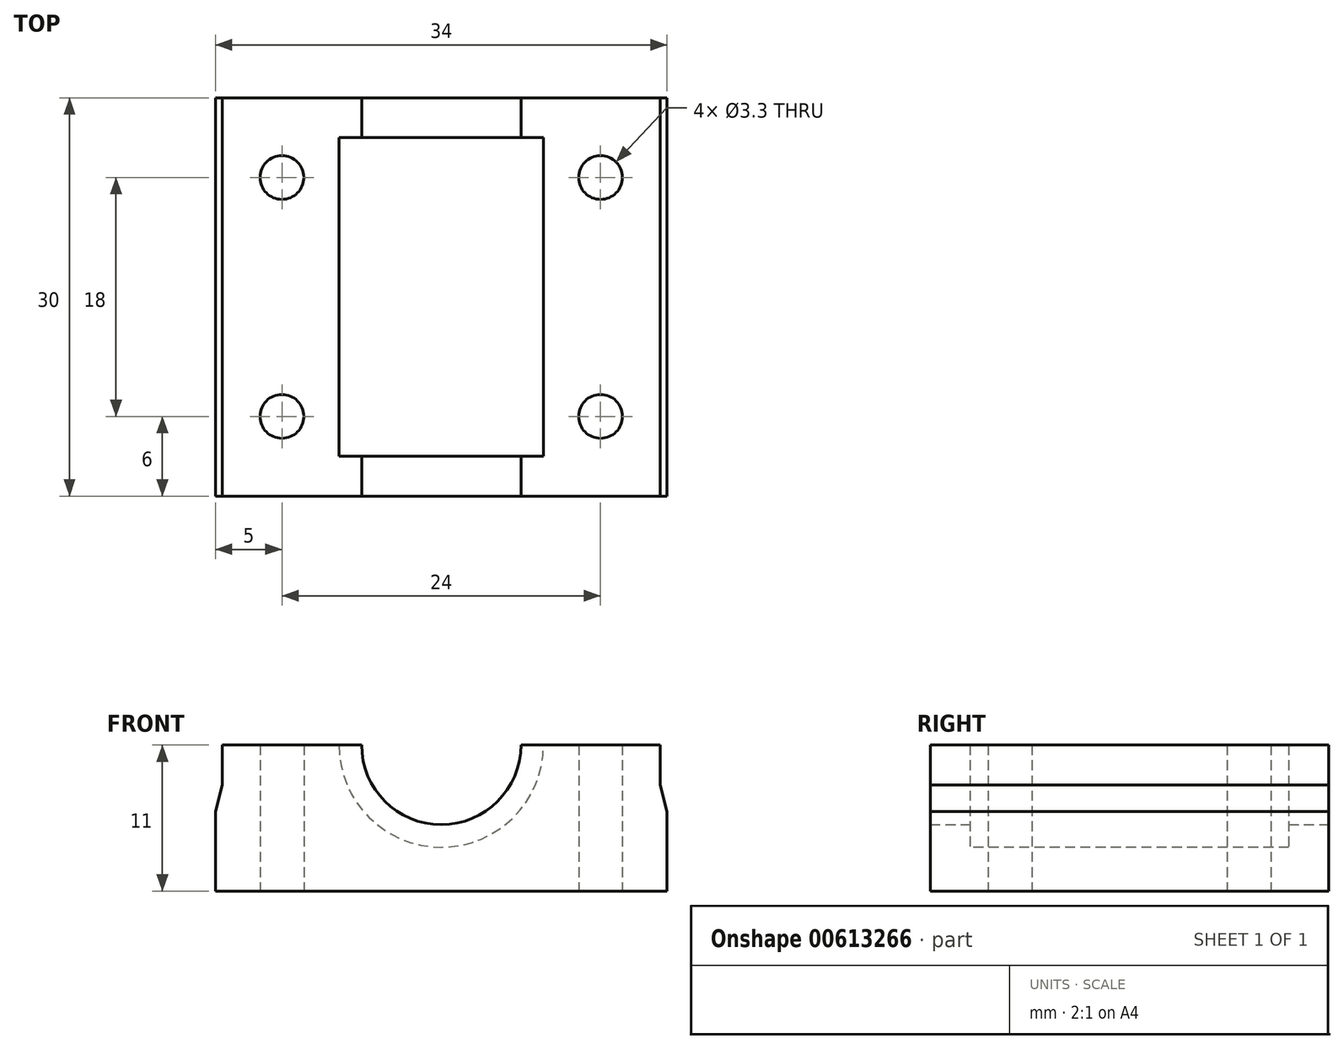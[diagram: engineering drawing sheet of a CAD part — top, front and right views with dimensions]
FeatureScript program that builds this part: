
annotation { "Feature Type Name" : "Feature", "Feature Type Description" : "" }
export const myFeature = defineFeature(function(context is Context, id is Id, definition is map)
    precondition{}
    {
        {
            var Q0;
            Q0=qCreatedBy(makeId("Front.planeOp"),FACE);
            var sketch = newSketch(context, id + "F0", { "sketchPlane" : qUnion([Q0])});
            skLineSegment(sketch, "E0", {"start": v(0, 0) * mm, "end": v(-5.45, 0) * mm});
            skLineSegment(sketch, "E1", {"start": v(-5.45, 0) * mm, "end": v(-9.5, 0) * mm});
            skLineSegment(sketch, "E2", {"start": v(-9.5, 0) * mm, "end": v(-17, 0) * mm});
            skLineSegment(sketch, "E3", {"start": v(-17, 0) * mm, "end": v(-17, 6) * mm});
            skLineSegment(sketch, "E4", {"start": v(-17, 6) * mm, "end": v(-16.5, 8) * mm});
            skLineSegment(sketch, "E5", {"start": v(-16.5, 8) * mm, "end": v(-16.5, 18) * mm});
            skLineSegment(sketch, "E6", {"start": v(-16.5, 18) * mm, "end": v(-9.5, 18) * mm});
            skLineSegment(sketch, "E7", {"start": v(-9.5, 18) * mm, "end": v(-3.5, 22) * mm});
            skLineSegment(sketch, "E8", {"start": v(-3.5, 22) * mm, "end": v(0, 22) * mm});
            skLineSegment(sketch, "E9", {"start": v(0, 22) * mm, "end": v(0, 0) * mm});
            skArc(sketch, "E10", {"start": v(0, 17) * mm, "mid": v(-6, 11) * mm, "end": v(0, 5) * mm});
            skLineSegment(sketch, "E11", {"start": v(-9.5, 29.22) * mm, "end": v(-9.5, -8.86) * mm, "construction": true});
            skLineSegment(sketch, "E12.MirrorCS", {"start": v(17, 6) * mm, "end": v(16.5, 8) * mm});
            skLineSegment(sketch, "E13.MirrorCS", {"start": v(0, 0) * mm, "end": v(5.45, 0) * mm});
            skLineSegment(sketch, "E14.MirrorCS", {"start": v(5.45, 0) * mm, "end": v(9.5, 0) * mm});
            skLineSegment(sketch, "E15.MirrorCS", {"start": v(9.5, 0) * mm, "end": v(17, 0) * mm});
            skLineSegment(sketch, "E16.MirrorCS", {"start": v(17, 0) * mm, "end": v(17, 6) * mm});
            skLineSegment(sketch, "E17.MirrorCS", {"start": v(16.5, 8) * mm, "end": v(16.5, 18) * mm});
            skLineSegment(sketch, "E18.MirrorCS", {"start": v(16.5, 18) * mm, "end": v(9.5, 18) * mm});
            skLineSegment(sketch, "E19.MirrorCS", {"start": v(9.5, 18) * mm, "end": v(3.5, 22) * mm});
            skLineSegment(sketch, "E20.MirrorCS", {"start": v(3.5, 22) * mm, "end": v(0, 22) * mm});
            skArc(sketch, "E21.MirrorCS", {"start": v(0, 17) * mm, "mid": v(6, 11) * mm, "end": v(0, 5) * mm});
            skCircle(sketch, "E22", {"center": v(0, 11) * mm, "radius": 7.5 * mm, "construction": true});
            skLineSegment(sketch, "E23", {"start": v(-16.5, 11) * mm, "end": v(16.5, 11) * mm});
            skLineSegment(sketch, "E24", {"start": v(-21.67, 8) * mm, "end": v(23.4, 8) * mm, "construction": true});
            skSolve(sketch);
        }
        {
            var Q0;
            {var subQ2=sQuery(id+"F0.wireOp",EDGE,"E0");Q0=makeQuery(id+"F0.imprint","IMPRINT",FACE,{"disambiguationData":[TD([[makeQuery(id+"F0.imprint","IMPRINT",EDGE,{"derivedFrom":subQ2}),-1.0]])]});}
            var Q1;
            Q1=makeQuery(id+"F0.imprint","IMPRINT",FACE,{"disambiguationData":[TD([[makeQuery(id+"F0.imprint","IMPRINT",EDGE,{"derivedFrom":sQuery(id+"F0.wireOp",EDGE,"E12.MirrorCS")}),1.0]])]});
            extrude(context, id + "F1", {"entities" : qUnion([Q0, Q1]), "endBound" : BoundingType.SYMMETRIC, "depth" : 30 * mm, "offsetDistance" : 25 * mm});
        }
        {
            var Q0;
            Q0=makeQuery(id+"F1.opExtrude","SWEPT_FACE",FACE,{"disambiguationData":[OSD([sQuery(id+"F0.wireOp",EDGE,"E2")])]});
            var sketch = newSketch(context, id + "F2", { "sketchPlane" : qUnion([Q0])});
            skPoint(sketch, "E25", {"position": v(-12, 9) * mm});
            skPoint(sketch, "E26", {"position": v(-12, -9) * mm});
            skPoint(sketch, "E27.MirrorP", {"position": v(12, 9) * mm});
            skPoint(sketch, "E28.MirrorP", {"position": v(12, -9) * mm});
            skLineSegment(sketch, "E29", {"start": v(-12, -30.48) * mm, "end": v(-12, 39.38) * mm, "construction": true});
            skSolve(sketch);
        }
        {
            var Q0;
            Q0=sQuery(id+"F2.wireOp",VERTEX,"E25");
            var Q1;
            Q1=sQuery(id+"F2.wireOp",VERTEX,"E26");
            var Q2;
            Q2=sQuery(id+"F2.wireOp",VERTEX,"E28.MirrorP");
            var Q3;
            Q3=sQuery(id+"F2.wireOp",VERTEX,"E27.MirrorP");
            var Q4;
            Q4=makeQuery(id+"F1.opExtrude","SWEPT_BODY",BODY,{"disambiguationData":[OSD([sQuery(id+"F0.wireOp",EDGE,"E0"),sQuery(id+"F0.wireOp",EDGE,"E1"),sQuery(id+"F0.wireOp",EDGE,"E2"),sQuery(id+"F0.wireOp",EDGE,"E3"),sQuery(id+"F0.wireOp",EDGE,"E4"),sQuery(id+"F0.wireOp",EDGE,"E5"),sQuery(id+"F0.wireOp",EDGE,"E6"),sQuery(id+"F0.wireOp",EDGE,"E7"),sQuery(id+"F0.wireOp",EDGE,"E8"),sQuery(id+"F0.wireOp",EDGE,"E10"),sQuery(id+"F0.wireOp",EDGE,"E12.MirrorCS"),sQuery(id+"F0.wireOp",EDGE,"E13.MirrorCS"),sQuery(id+"F0.wireOp",EDGE,"E14.MirrorCS"),sQuery(id+"F0.wireOp",EDGE,"E15.MirrorCS"),sQuery(id+"F0.wireOp",EDGE,"E16.MirrorCS"),sQuery(id+"F0.wireOp",EDGE,"E17.MirrorCS"),sQuery(id+"F0.wireOp",EDGE,"E18.MirrorCS"),sQuery(id+"F0.wireOp",EDGE,"E19.MirrorCS"),sQuery(id+"F0.wireOp",EDGE,"E20.MirrorCS"),sQuery(id+"F0.wireOp",EDGE,"E21.MirrorCS")])]});
            hole(context, id + "F3", {"style" : HoleStyle.SIMPLE, "endStyle" : HoleEndStyle.THROUGH, "standardTappedOrClearance" : lookupTablePath({ "standard" : "ISO", "fit" : "Normal", "size" : "M3", "type" : "Clearance" }), "standardBlindInLast" : lookupTablePath({ "fit" : "Standard", "standard" : "ISO", "size" : "M3", "type" : "Clearance" }), "holeDiameter" : 3.3 * mm, "majorDiameter" : 5 * mm, "isTappedThrough" : true, "tappedDepth" : 12 * mm, "tapClearance" : 3, "locations" : qUnion([Q0, Q1, Q2, Q3]), "scope" : qUnion([Q4])});
        }
        {
            var Q0;
            Q0=qCreatedBy(makeId("Front.planeOp"),FACE);
            var sketch = newSketch(context, id + "F4", { "sketchPlane" : qUnion([Q0])});
            skCircle(sketch, "E30", {"center": v(0, 11) * mm, "radius": 7.7 * mm});
            skSolve(sketch);
        }
        {
            var Q0;
            Q0=makeQuery(id+"F4.imprint","IMPRINT",FACE,{"disambiguationData":[TD([[makeQuery(id+"F4.imprint","IMPRINT",EDGE,{"derivedFrom":sQuery(id+"F4.wireOp",EDGE,"E30")}),1.0]])]});
            extrude(context, id + "F5", {"entities" : qUnion([Q0]), "operationType" : NewBodyOperationType.REMOVE, "endBound" : BoundingType.SYMMETRIC, "oppositeDirection" : true, "depth" : 24 * mm, "offsetDistance" : 25 * mm});
        }
    });
